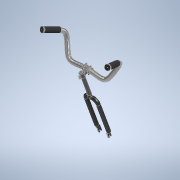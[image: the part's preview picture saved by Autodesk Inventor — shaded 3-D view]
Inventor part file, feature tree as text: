
AUTODESK INVENTOR PART (.ipt)
format: ipt  version: 2021 (Build 250183000, 183)  size: 5,211,648 bytes
history: native  units: in
note: dims shown in document units (in); Inventor stores cm internally (conversion verified against a paired STEP export)
features: plane x34, sketch x28, other x15, extrude x14, projected_geometry x9, loft x5, fillet x4, mirror x4, hole x2, split x2, sweep x1, move_body x1, chamfer x1, revolve x1
ambient origin geometry x8: Origin, YZ Plane, XZ Plane, XY Plane, X Axis, Y Axis, Z Axis, Center Point
bodies: Solid4 (feature_tree)
feature tree (121):
  sketch  "3D Sketch1"
  plane  "Work Plane6"
  sweep  "Sweep3"
  plane  "Work Plane4"
  plane  "Work Plane5"
  sketch  "Sketch14"  dims[d24=1.66in d25=0.0in d26=0.0in]
  sketch  "Sketch15"  dims[d28=2.0472in d29=0.0in d30=90.0deg d31=0.0in d32=90.0deg]
  loft  "Loft1"
  loft  "Loft2"
  plane  "Work Plane7"
  sketch  "Sketch16"  dims[d33=0.0in d34=90.0deg d35=0.0in d36=90.0deg d37=0.0in d42=180.0deg]
  plane  "Work Plane8"
  extrude  "Extrusion2"  TaperAngle=180.0deg  [1 undecoded]
  extrude  "Extrusion3"  Depth=1.378in TaperAngle=0.0deg
  plane  "Work Plane9"
  extrude  "Extrusion4"  Depth=1.7225in TaperAngle=0.0deg
  extrude  "Extrusion5"  Depth=1.1024in
  plane  "Work Plane22"
  sketch  "Sketch33"  dims[d112=0.3937in d113=0.0in d114=0.3937in d115=0.0in]
  plane  "Work Plane23"
  extrude  "Extrusion10"  Depth=0.1969in
  plane  "Work Plane19"
  plane  "Work Plane20"
  extrude  "Extrusion11"  Depth=0.4331in
  fillet  "Fillet1"  Radius=0.0197in
  plane  "Work Plane24"
  plane  "Work Plane25"
  hole  "Hole1"  [1 undecoded]
  mirror  "Mirror5"
  other  "Work Axis4"
  mirror  "Mirror3"
  plane  "Work Plane34"
  extrude  "Extrusion13"  Depth=0.3937in TaperAngle=0.0deg
  fillet  "Fillet2"  Radius=0.0984in
  plane  "Work Plane35"
  hole  "Hole2"  [1 undecoded]
  plane  "Work Plane36"
  sketch  "Sketch44"  dims[d149=1.1024in]
  split  "Split2"
  plane  "Work Plane26"
  split  "Split1"
  other  "Work Axis1"
  move_body  "Move Body2"
  plane  "Work Plane10"
  plane  "Work Plane11"
  plane  "Work Plane12"
  extrude  "Extrusion6"  [1 undecoded]
  sketch  "Sketch23"  dims[d73=0.3937in d74=0.0in d79=0.4331in d80=0.0197in]
  loft  "Loft5"
  loft  "Loft8"
  plane  "Work Plane13"
  extrude  "Extrusion8"  TaperAngle=180.0deg  [1 undecoded]
  other  "Work Axis5"
  other  "Bend Part2"
  plane  "Work Plane30"
  sketch  "Sketch36"  dims[d121=2.0in d122=0.1575in d123=0.0787in d124=90.0deg d125=1.66in d126=0.8108in]
  loft  "Loft10"
  plane  "Work Plane41"
  plane  "Work Plane31"
  extrude  "Extrusion17"  TaperAngle=90.0deg  [1 undecoded]
  plane  "Work Plane32"
  extrude  "Extrusion12"  Depth=1.38in
  chamfer  "Chamfer1"  Distance=0.7874in
  fillet  "Fillet4"  Radius=1.9685in
  mirror  "Mirror6"
  plane  "Work Plane33"
  sketch  "Sketch41"  dims[d138=1.38in d139=1.66in]
  plane  "Work Plane37"
  revolve  "Revolution2"  [1 undecoded]
  plane  "Work Plane38"
  extrude  "Extrusion14"  TaperAngle=0.0deg  [1 undecoded]
  plane  "Work Plane39"
  extrude  "Extrusion15"  Depth=0.1969in
  fillet  "Fillet3"  Radius=0.3937in
  plane  "Work Plane40"
  extrude  "Extrusion16"  Depth=0.4921in
  mirror  "Mirror7"
  sketch  "Sketch13"  dims[d19=0.0in d21=1.378in d23=1.38in]
  other  "Caña Dirección"
  sketch  "Sketch17"  dims[d43=0.3937in d44=0.0in d45=1.378in d46=0.0in]
  sketch  "Sketch18"  dims[d48=180.0deg d49=1.7225in d50=0.0in]
  sketch  "Sketch19"  dims[d53=0.8661in d54=0.0in d55=1.1024in]
  sketch  "Sketch20"  dims[d57=180.0deg d60=0.1969in]
  other  "Tubo Tenedor Central"
  sketch  "Sketch25"  dims[d85=14.9449in d86=1.38in]
  other  "Tubo Tenedor Der"
  plane  "Work Plane18"
  sketch  "Sketch32"  dims[d94=0.0in d95=90.0deg d96=0.0in d97=90.0deg d98=0.3937in d99=0.0in d105=0.0984in]
  plane  "Work Plane21"
  sketch  "Sketch34"  dims[d116=0.1969in d117=-1.0236in]
  plane  "Work Plane27"
  plane  "Work Plane28"
  sketch  "Sketch35"  dims[d119=0.1181in]
  other  "Pattern of Tubo Tenedor Der:2"
  other  "Tubo Tenedor Izq"
  plane  "Work Plane29"
  sketch  "Sketch37"  dims[d127=0.4921in d128=0.0in]
  sketch  "Sketch40"  dims[d131=90.0deg d132=180.0deg]
  sketch  "Sketch42"  dims[d140=1.66in d144=90.0deg]
  sketch  "Sketch43"  dims[d145=180.0deg d146=1.38in]
  sketch  "Sketch45"  dims[d152=1.0817in]
  other  "Copa Tenedor"
  sketch  "Sketch46"  dims[d153=90.0deg d154=0.0in d155=0.7874in d180=1.9685in]
  other  "Mango Izq"
  sketch  "Sketch47"  dims[d193=0.1969in d196=0.0in d197=0.0in]
  sketch  "Sketch48"  dims[d198=0.0in d205=0.0in]
  other  "Pattern of Mango Izq:3"
  other  "Mango Der"
  sketch  "Sketch49"  dims[d206=0.9843in d208=0.7874in d210=0.1969in d211=0.3937in d212=0.0in]
  sketch  "Sketch50"  dims[d215=0.3369in d216=0.4921in d218=0.5629in d219=0.2362in d220=0.1181in d221=0.0in d222=0.1969in d223=0.2362in d224=0.1575in d225=0.0787in d226=90.0deg d227=1.66in d228=0.8108in d229=0.0in d236=0.0in d237=90.0deg d238=0.0in d239=90.0deg d246=0.14in d247=0.315in d248=0.83in d249=90.0deg d250=-3.937in d251=1.9685in d252=5.9055in d253=0.0in d254=0.0in d255=2.1654in d256=0.3937in d257=0.0in d258=0.0787in d259=0.0in d260=0.1575in d261=0.3937in d262=0.0in d265=0.0in d266=90.0deg d269=0.3937in d270=0.0in d271=90.0deg d272=0.0in d273=0.3937in d274=0.0in d275=0.69in d276=0.7815in d277=0.1969in d278=0.0787in d279=45.0deg d280=0.0787in d141=0.0344in]
  projected_geometry  "Project Cut Edges2"
  projected_geometry  "Project Cut Edges3"
  projected_geometry  "Project Cut Edges4"
  projected_geometry  "Project Cut Edges5"
  projected_geometry  "Project Cut Edges6"
  projected_geometry  "Project Cut Edges7"
  other  "Potencia Del"
  other  "Potencia Tras"
  projected_geometry  "Project Cut Edges10"
  projected_geometry  "Project Cut Edges11"
  projected_geometry  "Project Cut Edges12"
note: 8 required parameter values undecoded (feature->parameter linkage not recoverable at this tier; creation-order binding heuristic only, values carry confidence <= 0.55)